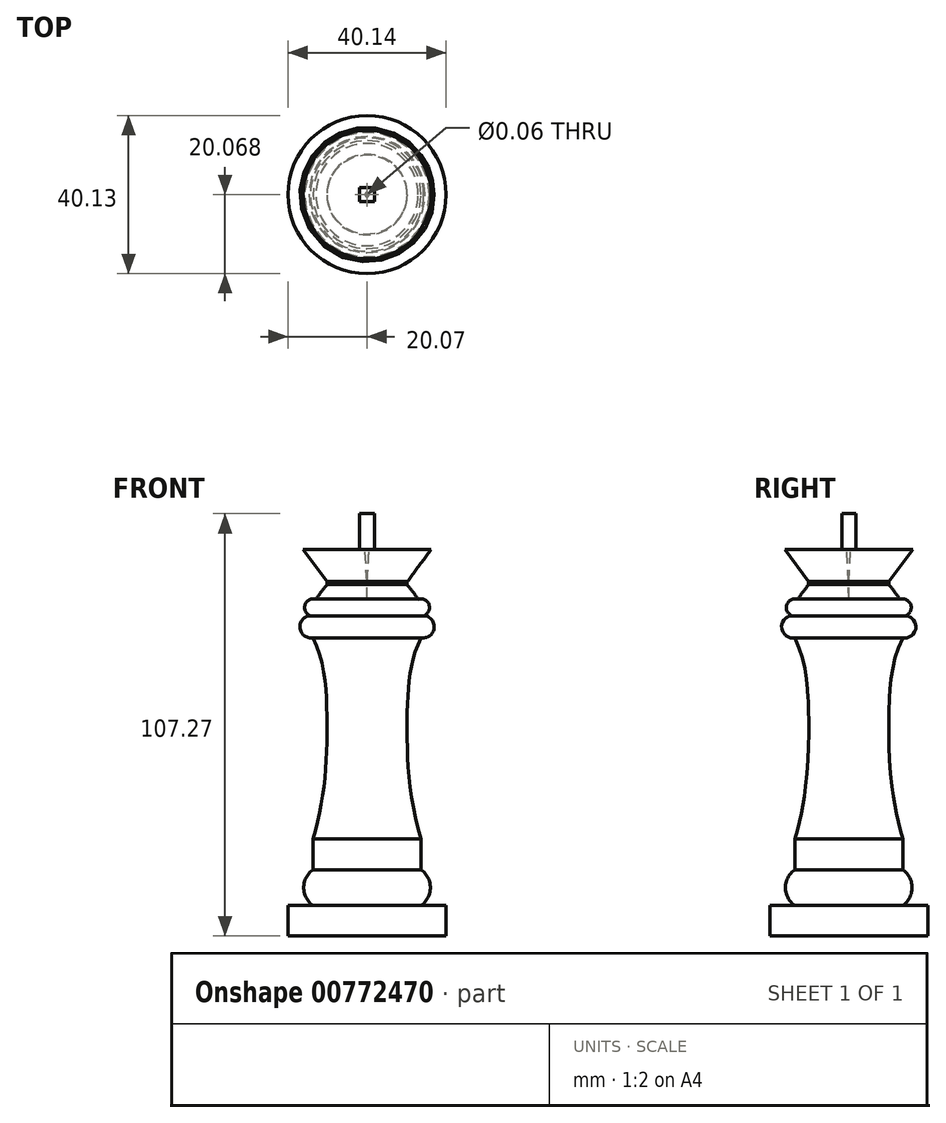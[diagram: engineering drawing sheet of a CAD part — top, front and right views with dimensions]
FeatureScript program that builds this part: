
annotation { "Feature Type Name" : "Feature", "Feature Type Description" : "" }
export const myFeature = defineFeature(function(context is Context, id is Id, definition is map)
    precondition{}
    {
        {
            var Q0;
            Q0=qCreatedBy(makeId("Right.planeOp"),FACE);
            var sketch = newSketch(context, id + "F0", { "sketchPlane" : qUnion([Q0])});
            skLineSegment(sketch, "E0", {"start": v(-0.03, 0) * mm, "end": v(20.03, 0) * mm});
            skLineSegment(sketch, "E1", {"start": v(20.03, 0) * mm, "end": v(20.03, 7.73) * mm});
            skLineSegment(sketch, "E2", {"start": v(7.34, 7.73) * mm, "end": v(20.03, 7.73) * mm});
            skArc(sketch, "E3", {"start": v(13.69, 7.73) * mm, "mid": v(16.06, 12.28) * mm, "end": v(13.69, 16.83) * mm});
            skPoint(sketch, "E3.endSnap0", {"position": v(13.69, 7.73) * mm});
            skLineSegment(sketch, "E4", {"start": v(13.69, 16.83) * mm, "end": v(13.69, 24.67) * mm});
            skFitSpline(sketch, "E5", {"points": [v(13.69, 24.67) * mm, v(10.18, 56.81) * mm, v(13.69, 75.73) * mm], "startDerivative": vector(-18.7, 61.39) * mm, "endDerivative": vector(20.18, 41.56) * mm});
            skArc(sketch, "E6", {"start": v(13.69, 75.73) * mm, "mid": v(16.98, 78.04) * mm, "end": v(14.67, 81.33) * mm});
            skLineSegment(sketch, "E7", {"start": v(14.67, 81.33) * mm, "end": v(12.88, 81.33) * mm});
            skArc(sketch, "E8", {"start": v(14.37, 81.33) * mm, "mid": v(15.7, 84.16) * mm, "end": v(12.88, 85.5) * mm});
            skLineSegment(sketch, "E9", {"start": v(-0.03, 85.5) * mm, "end": v(12.88, 85.5) * mm});
            skLineSegment(sketch, "E10", {"start": v(-0.03, 85.5) * mm, "end": v(-0.03, 0) * mm});
            skPoint(sketch, "E11.end.orphan", {"position": v(-12.94, 85.5) * mm});
            skArc(sketch, "E12", {"start": v(12.96, 85.5) * mm, "mid": v(11.61, 87.4) * mm, "end": v(10.18, 89.23) * mm});
            skLineSegment(sketch, "E13", {"start": v(0, 89.23) * mm, "end": v(10.18, 89.23) * mm});
            skLineSegment(sketch, "E14", {"start": v(-0.03, 85.5) * mm, "end": v(0, 89.23) * mm});
            skPoint(sketch, "E15.end.orphan", {"position": v(0, 89.23) * mm});
            skPoint(sketch, "E16.start.orphan", {"position": v(7.63, 89.23) * mm});
            skPoint(sketch, "E17.orphan", {"position": v(15.25, 89.23) * mm});
            skLineSegment(sketch, "E18", {"start": v(0, 90) * mm, "end": v(0, 89.23) * mm});
            skPoint(sketch, "E19.start.orphan", {"position": v(0, 106.91) * mm});
            skLineSegment(sketch, "E20.bottom", {"start": v(10.18, 89.23) * mm, "end": v(0, 89.23) * mm});
            skLineSegment(sketch, "E20.top", {"start": v(10.18, 90) * mm, "end": v(0, 90) * mm});
            skLineSegment(sketch, "E20.left", {"start": v(10.18, 89.23) * mm, "end": v(10.18, 90) * mm});
            skLineSegment(sketch, "E20.right", {"start": v(0, 89.23) * mm, "end": v(0, 90) * mm});
            skPoint(sketch, "E21.start.orphan", {"position": v(12.96, 94.9) * mm});
            skPoint(sketch, "E22.start.orphan", {"position": v(0, 94.9) * mm});
            skLineSegment(sketch, "E23", {"start": v(10.18, 90) * mm, "end": v(16.24, 98.17) * mm});
            skLineSegment(sketch, "E24", {"start": v(16.24, 98.17) * mm, "end": v(0.48, 98.17) * mm});
            skLineSegment(sketch, "E25", {"start": v(0.48, 98.17) * mm, "end": v(0, 90) * mm});
            skSolve(sketch);
        }
        {
            var Q0;
            Q0 = qSketchRegion(id + "F0", true);
            var Q1;
            Q1=sQuery(id+"F0.wireOp",EDGE,"E10");
            revolve(context, id + "F1", {"surfaceOperationType" : NewSurfaceOperationType.NEW, "entities" : qUnion([Q0]), "axis" : qUnion([Q1]), "revolveType" : RevolveType.FULL});
        }
        {
            var Q0;
            Q0=makeQuery(id+"F1.opRevolve","SWEPT_FACE",FACE,{"disambiguationData":[OSD([sQuery(id+"F0.wireOp",EDGE,"E24")])]});
            var sketch = newSketch(context, id + "F2", { "sketchPlane" : qUnion([Q0])});
            skLineSegment(sketch, "E26.bottom", {"start": v(-1.92, -1.75) * mm, "end": v(1.92, -1.75) * mm});
            skLineSegment(sketch, "E26.top", {"start": v(-1.92, 1.75) * mm, "end": v(1.92, 1.75) * mm});
            skLineSegment(sketch, "E26.left", {"start": v(-1.92, -1.75) * mm, "end": v(-1.92, 1.75) * mm});
            skLineSegment(sketch, "E26.right", {"start": v(1.92, -1.75) * mm, "end": v(1.92, 1.75) * mm});
            skPoint(sketch, "E26.middle", {"position": v(0, 0) * mm});
            skSolve(sketch);
        }
        {
            var Q0;
            Q0 = qSketchRegion(id + "F2", true);
            extrude(context, id + "F3", {"entities" : qUnion([Q0]), "operationType" : NewBodyOperationType.ADD, "depth" : 9.1 * mm, "offsetDistance" : 25 * mm});
        }
    });
